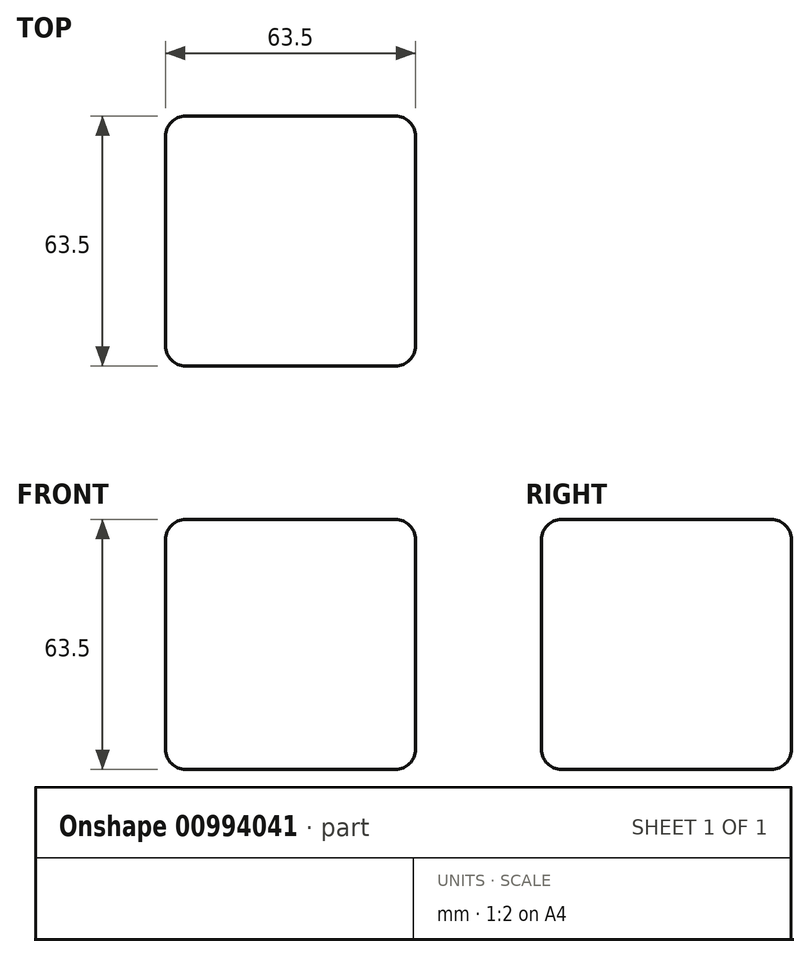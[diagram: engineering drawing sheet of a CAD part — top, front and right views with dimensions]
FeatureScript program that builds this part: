
annotation { "Feature Type Name" : "Feature", "Feature Type Description" : "" }
export const myFeature = defineFeature(function(context is Context, id is Id, definition is map)
    precondition{}
    {
        {
            var Q0;
            Q0=qCreatedBy(makeId("Top.planeOp"),FACE);
            var sketch = newSketch(context, id + "F0", { "sketchPlane" : qUnion([Q0])});
            skLineSegment(sketch, "E0.bottom", {"start": v(-31.75, 31.75) * mm, "end": v(31.75, 31.75) * mm});
            skLineSegment(sketch, "E0.top", {"start": v(-31.75, -31.75) * mm, "end": v(31.75, -31.75) * mm});
            skLineSegment(sketch, "E0.left", {"start": v(-31.75, 31.75) * mm, "end": v(-31.75, -31.75) * mm});
            skLineSegment(sketch, "E0.right", {"start": v(31.75, 31.75) * mm, "end": v(31.75, -31.75) * mm});
            skPoint(sketch, "E0.middle", {"position": v(0, 0) * mm});
            skSolve(sketch);
        }
        {
            var Q0;
            Q0=makeQuery(id+"F0.imprint","IMPRINT",FACE,{"disambiguationData":[TD([[makeQuery(id+"F0.imprint","IMPRINT",EDGE,{"derivedFrom":sQuery(id+"F0.wireOp",EDGE,"E0.bottom")}),-1.0]])]});
            extrude(context, id + "F1", {"entities" : qUnion([Q0]), "depth" : 63.5 * mm, "offsetDistance" : 25.4 * mm});
        }
        {
            var Q0;
            Q0=makeQuery(id+"F1.opExtrude","SWEPT_FACE",FACE,{"disambiguationData":[OSD([sQuery(id+"F0.wireOp",EDGE,"E0.bottom")])]});
            var Q1;
            Q1=makeQuery(id+"F1.opExtrude","SWEPT_FACE",FACE,{"disambiguationData":[OSD([sQuery(id+"F0.wireOp",EDGE,"E0.left")])]});
            var Q2;
            Q2=makeQuery(id+"F1.opExtrude","SWEPT_FACE",FACE,{"disambiguationData":[OSD([sQuery(id+"F0.wireOp",EDGE,"E0.right")])]});
            var Q3;
            Q3=makeQuery(id+"F1.opExtrude","CAP_FACE",FACE,{"disambiguationData":[OSD([sQuery(id+"F0.wireOp",EDGE,"E0.bottom"),sQuery(id+"F0.wireOp",EDGE,"E0.top"),sQuery(id+"F0.wireOp",EDGE,"E0.left"),sQuery(id+"F0.wireOp",EDGE,"E0.right")])],"isStart":false});
            var Q4;
            Q4=makeQuery(id+"F1.opExtrude","CAP_FACE",FACE,{"disambiguationData":[OSD([sQuery(id+"F0.wireOp",EDGE,"E0.bottom"),sQuery(id+"F0.wireOp",EDGE,"E0.top"),sQuery(id+"F0.wireOp",EDGE,"E0.left"),sQuery(id+"F0.wireOp",EDGE,"E0.right")])],"isStart":true});
            fillet(context, id + "F2", {"entities" : qUnion([Q0, Q1, Q2, Q3, Q4]), "radius" : 5.08 * mm, "tangentPropagation" : true, "allowEdgeOverflow" : false});
        }
    });
